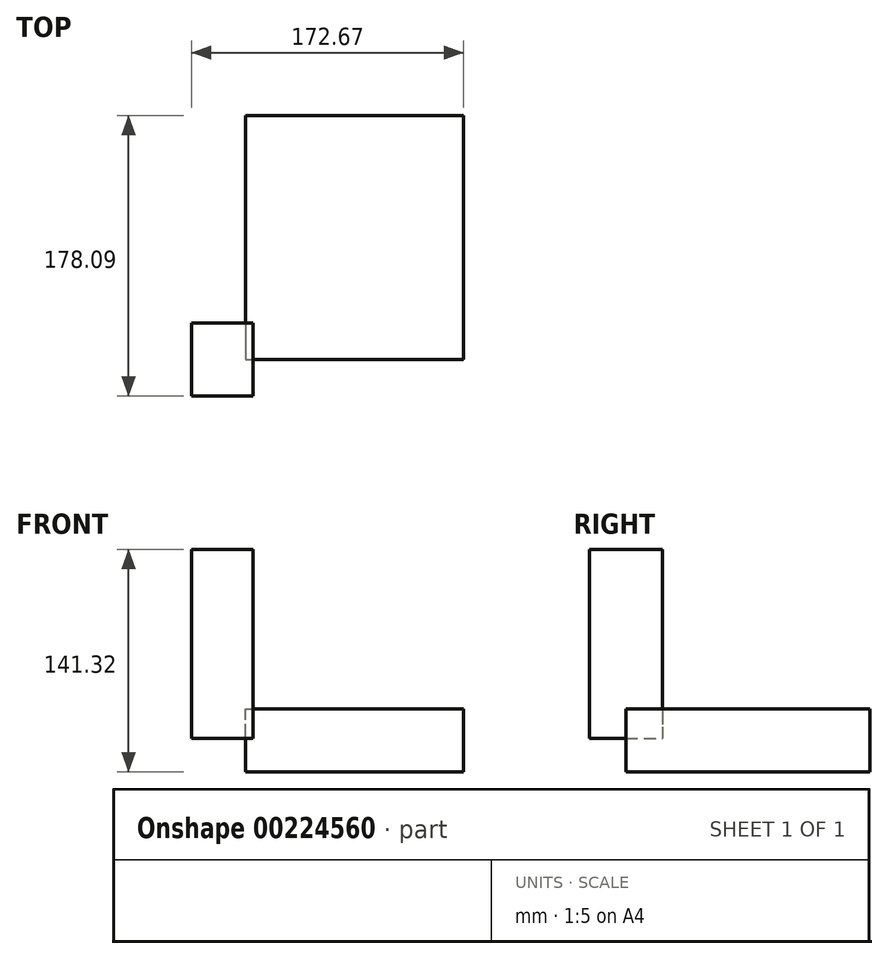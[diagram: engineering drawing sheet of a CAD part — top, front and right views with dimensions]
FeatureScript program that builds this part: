
annotation { "Feature Type Name" : "Feature", "Feature Type Description" : "" }
export const myFeature = defineFeature(function(context is Context, id is Id, definition is map)
    precondition{}
    {
        {
            var Q0;
            Q0=qCreatedBy(makeId("Top.planeOp"),FACE);
            var sketch = newSketch(context, id + "F0", { "sketchPlane" : qUnion([Q0])});
            skLineSegment(sketch, "E0.bottom", {"start": v(-106.62, -23.15) * mm, "end": v(-67.74, -23.15) * mm});
            skLineSegment(sketch, "E0.top", {"start": v(-106.62, 23.26) * mm, "end": v(-67.74, 23.26) * mm});
            skLineSegment(sketch, "E0.left", {"start": v(-106.62, -23.15) * mm, "end": v(-106.62, 23.26) * mm});
            skLineSegment(sketch, "E0.right", {"start": v(-67.74, -23.15) * mm, "end": v(-67.74, 23.26) * mm});
            skSolve(sketch);
        }
        {
            var Q0;
            Q0 = qSketchRegion(id + "F0", true);
            extrude(context, id + "F1", {"entities" : qUnion([Q0]), "depth" : 25.4 * mm});
        }
        {
            var Q0;
            Q0=makeQuery(id+"F1.opExtrude","CAP_FACE",FACE,{"disambiguationData":[OSD([sQuery(id+"F0.wireOp",EDGE,"E0.bottom"),sQuery(id+"F0.wireOp",EDGE,"E0.top"),sQuery(id+"F0.wireOp",EDGE,"E0.left"),sQuery(id+"F0.wireOp",EDGE,"E0.right")])],"isStart":false});
            extrude(context, id + "F2", {"entities" : qUnion([Q0]), "operationType" : NewBodyOperationType.ADD, "depth" : 94.49 * mm});
        }
        {
            var Q0;
            Q0=qCreatedBy(makeId("Front.planeOp"),FACE);
            var sketch = newSketch(context, id + "F3", { "sketchPlane" : qUnion([Q0])});
            skLineSegment(sketch, "E1.bottom", {"start": v(-72.49, -21.43) * mm, "end": v(66.05, -21.43) * mm});
            skLineSegment(sketch, "E1.top", {"start": v(-72.49, 18.56) * mm, "end": v(66.05, 18.56) * mm});
            skLineSegment(sketch, "E1.left", {"start": v(-72.49, -21.43) * mm, "end": v(-72.49, 18.56) * mm});
            skLineSegment(sketch, "E1.right", {"start": v(66.05, -21.43) * mm, "end": v(66.05, 18.56) * mm});
            skSolve(sketch);
        }
        {
            var Q0;
            Q0 = qSketchRegion(id + "F3", true);
            extrude(context, id + "F4", {"entities" : qUnion([Q0]), "oppositeDirection" : true, "depth" : 154.94 * mm});
        }
    });
